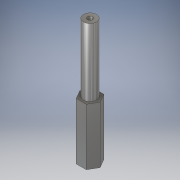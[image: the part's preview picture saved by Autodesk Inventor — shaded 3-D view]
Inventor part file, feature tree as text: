
AUTODESK INVENTOR PART (.ipt)
format: ipt  version: 2017 SP1 (Build 210196100, 196)  size: 110,592 bytes
history: native  units: in
note: dims shown in document units (in); Inventor stores cm internally (conversion verified against a paired STEP export)
features: extrude x2, sketch x2
ambient origin geometry x8: Origin, YZ Plane, XZ Plane, XY Plane, X Axis, Y Axis, Z Axis, Center Point
bodies: Solid1 (feature_tree)
feature tree (4):
  extrude  "Extrusion1"  Depth=1.625in TaperAngle=0.0deg
  extrude  "Extrusion2"  Depth=1.9375in TaperAngle=0.0deg
  sketch  "Sketch1"  dims[d0=0.5in d1=1.625in d2=0.0in]
  sketch  "Sketch2"  dims[d3=0.375in d4=1.9375in d5=0.0in d6=0.15in]
